# Revit family: Faucet-Wall_Mount-KOHLER-Purist-K-T11841
name_source: partatom
category: Plumbing Fixtures
revit_build: Autodesk Revit 2015 (Build: 20140606_1530(x64)
units: mm (PartAtom-declared; Revit-internal decimal feet)

## types (2) — shared parameters
ADA Compliant = Yes
Assembly Code = D2020
CW Connection = No
Cold Water Inlet = Cold Water Inlet
Date Modified = 01/15/2018
Default Elevation = 36"
Description = Wall-mount commercial bathroom sink faucet trim with 6Inch 90-degree spout and Insight™ technology
Faucet Hole Spacing = 0"
Flow Rate = 1 GPM
HW Connection = Yes
Height = 4 15/16"
Hot Water Inlet = Hot Water Inlet
Length = 6 3/32"
Manufacturer = KOHLER Co.
MasterFormat 1995 = 15410
MasterFormat 2004 = 22.41.39
Material = Brass construction
Pressure = 0.00 psi
Product Documentation Link = https://www.us.kohler.com
Product Name = Purist
Product Page URL = http://www.us.kohler.com
Spout Reach = 5 11/16"
URL = https://www.us.kohler.com
Vent Connection = No
Waste Connection = No
Waste Water Outlet = Waste Water Outlet
Width = 1 31/32"

## per-type parameters (varying)
| type | Finish | Model | Type |
| CP-Polished Chrome | Kohler-Metal-CP-Polished_Chrome | K-T11841-CP | 1 |
| VS-Stainless Steel | Kohler-Metal-VS-Vibrant_Stainless | K-T11841-VS | 2 |

## geometry (parser evidence)
native form markers: Sweep x6
no freeform markers — native parametric forms only
